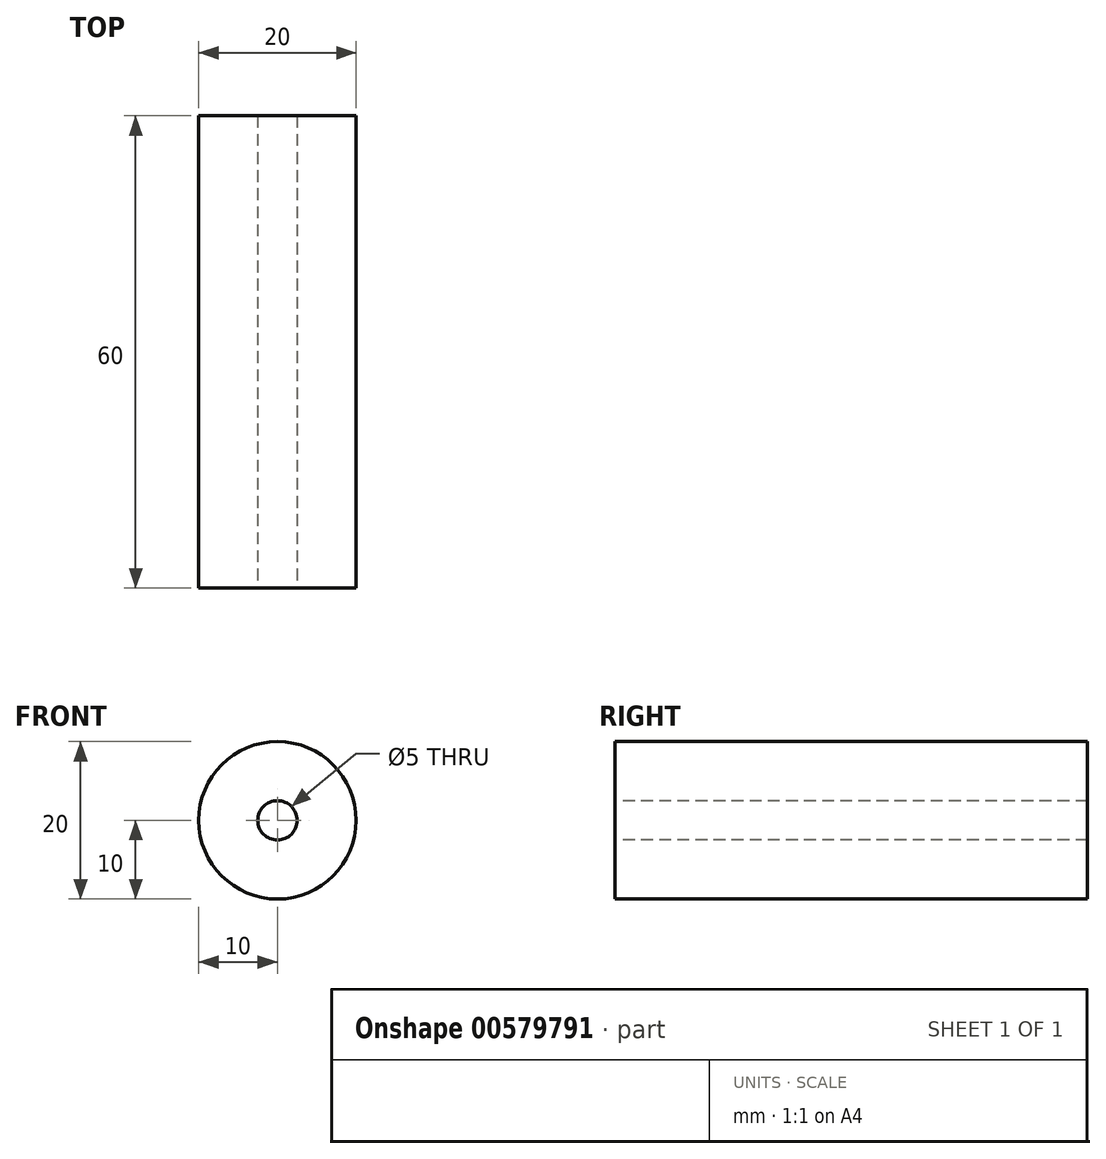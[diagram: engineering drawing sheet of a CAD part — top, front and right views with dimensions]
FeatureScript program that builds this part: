
annotation { "Feature Type Name" : "Feature", "Feature Type Description" : "" }
export const myFeature = defineFeature(function(context is Context, id is Id, definition is map)
    precondition{}
    {
        {
            var Q0;
            Q0=qCreatedBy(makeId("Front.planeOp"),FACE);
            var sketch = newSketch(context, id + "F0", { "sketchPlane" : qUnion([Q0])});
            skCircle(sketch, "E0", {"center": v(0, 0) * mm, "radius": 10 * mm});
            skSolve(sketch);
        }
        {
            var Q0;
            Q0=makeQuery(id+"F0.imprint","IMPRINT",FACE,{"disambiguationData":[TD([[makeQuery(id+"F0.imprint","IMPRINT",EDGE,{"derivedFrom":sQuery(id+"F0.wireOp",EDGE,"E0")}),1.0]])]});
            extrude(context, id + "F1", {"entities" : qUnion([Q0]), "depth" : 60 * mm, "offsetDistance" : 25.4 * mm});
        }
        {
            var Q0;
            Q0=makeQuery(id+"F1.opExtrude","CAP_FACE",FACE,{"disambiguationData":[OSD([sQuery(id+"F0.wireOp",EDGE,"E0")])],"isStart":false});
            var sketch = newSketch(context, id + "F2", { "sketchPlane" : qUnion([Q0])});
            skCircle(sketch, "E1.0", {"center": v(0, 0) * mm, "radius": 10 * mm});
            skSolve(sketch);
        }
        {
            var Q0;
            Q0=sQuery(id+"F2.wireOp",VERTEX,"E1.0.center");
            var Q1;
            Q1=makeQuery(id+"F1.opExtrude","SWEPT_BODY",BODY,{"disambiguationData":[OSD([sQuery(id+"F0.wireOp",EDGE,"E0")])]});
            hole(context, id + "F3", {"style" : HoleStyle.SIMPLE, "endStyle" : HoleEndStyle.THROUGH, "standardTappedOrClearance" : lookupTablePath({ "standard" : "ISO", "size" : "5", "type" : "Drilled" }), "standardBlindInLast" : lookupTablePath({ "standard" : "ISO", "size" : "5", "type" : "Drilled" }), "holeDiameter" : 5 * mm, "isTappedThrough" : true, "tappedDepth" : 12.7 * mm, "tapClearance" : 3, "locations" : qUnion([Q0]), "scope" : qUnion([Q1])});
        }
    });
